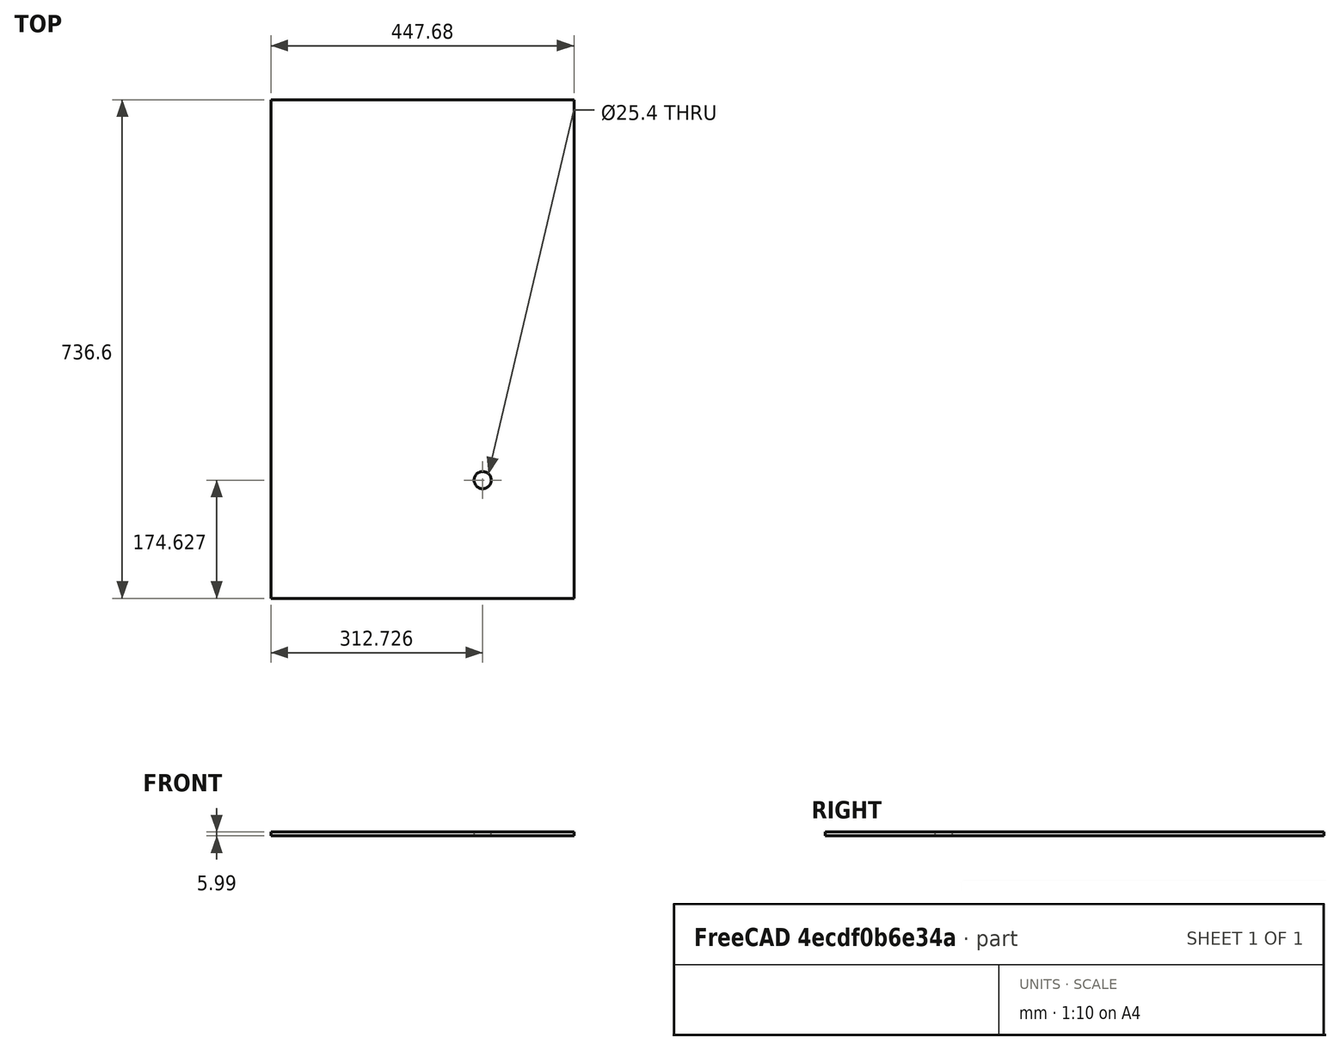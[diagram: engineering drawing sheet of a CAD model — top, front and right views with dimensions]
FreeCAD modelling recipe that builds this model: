
FCSTD DOCUMENT  (FreeCAD 0.19R24267 (Git))
Label: Inv1-P12
License: All rights reserved
LicenseURL: http://en.wikipedia.org/wiki/All_rights_reserved
objects: TechDraw::DrawViewDimension×6, TechDraw::DrawProjGroupItem×2, TechDraw::DrawHatch×2, TechDraw::DrawViewAnnotation×2, Sketcher::SketchObject×1, Part::Extrusion×1, TechDraw::DrawSVGTemplate×1, TechDraw::DrawProjGroup×1, TechDraw::DrawPage×1
note: 2 computed .brp shape members not serialized (recipe doc carries the construction recipe); baked Part::Feature solids carry a one-line shape summary decoded from their .brp

FEATURE [Sketcher::SketchObject] Sketch
  FullyConstrained = false
  sketch-geometry (5):
    g0: LineSegment StartX=-121.759 StartY=252.582 StartZ=0 EndX=325.916 EndY=252.582 EndZ=0
    g1: LineSegment StartX=325.916 StartY=252.582 StartZ=0 EndX=325.916 EndY=-484.018 EndZ=0
    g2: LineSegment StartX=325.916 StartY=-484.018 StartZ=0 EndX=-121.759 EndY=-484.018 EndZ=0
    g3: LineSegment StartX=-121.759 StartY=-484.018 StartZ=0 EndX=-121.759 EndY=252.582 EndZ=0
    g4: Circle CenterX=190.966 CenterY=-309.393 CenterZ=0 NormalX=0 NormalY=0 NormalZ=1 AngleXU=0 Radius=12.7
  constraints (13):
    c: Coincident(g0,g1)
    c: Coincident(g1,g2)
    c: Coincident(g2,g3)
    c: Coincident(g3,g0)
    c: Horizontal(g0)
    c: Horizontal(g2)
    c: Vertical(g1)
    c: Vertical(g3)
    c: DistanceX(g0,g0) = 447.675
    c: DistanceY(g3,g3) = 736.6
    c: Distance(g4,g1) = 134.95
    c: Distance(g4,g2) = 174.625
    c: Diameter(g4) = 25.4
FEATURE [Part::Extrusion] Extrude
  Base = -> Sketch
  Dir = (0,0,1)
  DirMode = 2
  FaceMakerClass = Part::FaceMakerBullseye
  LengthFwd = 5.9944
  LengthRev = 0
  Solid = true
  Symmetric = false
FEATURE [TechDraw::DrawSVGTemplate] Template
  Height = 215.9
  Orientation = 1
  Width = 279.4
FEATURE [TechDraw::DrawProjGroupItem] ProjItem  label="Front"
  CoarseView = false
  Direction = (0,0,1)
  Focus = 100
  HardHidden = false
  IsoCount = 0
  IsoHidden = false
  IsoVisible = false
  LockPosition = true
  Perspective = false
  Rotation = 0
  RotationVector = (1,0,0)
  Scale = 0.2
  ScaleType = 2
  SeamHidden = false
  SeamVisible = true
  SmoothHidden = false
  SmoothVisible = true
  Source = -> [Extrude]
  Type = 0
  X = 0
  XDirection = (1,0,0)
  Y = 0
FEATURE [TechDraw::DrawProjGroupItem] ProjItem001  label="Left"
  CoarseView = false
  Direction = (-1,0,1e-16)
  Focus = 100
  HardHidden = false
  IsoCount = 0
  IsoHidden = false
  IsoVisible = false
  LockPosition = false
  Perspective = false
  Rotation = 0
  RotationVector = (1,0,0)
  Scale = 0.2
  ScaleType = 2
  SeamHidden = false
  SeamVisible = true
  SmoothHidden = false
  SmoothVisible = true
  Source = -> [Extrude]
  Type = 1
  X = 81.5403
  XDirection = (1e-16,0,1)
  Y = 0
FEATURE [TechDraw::DrawProjGroup] ProjGroup
  Anchor = -> ProjItem
  AutoDistribute = true
  LockPosition = false
  ProjectionType = 0
  Rotation = 0
  Scale = 0.2
  ScaleType = 2
  Source = -> [Extrude]
  Views = -> [ProjItem,ProjItem001]
  X = 129.402
  Y = 104.062
  spacingX = 15.0114
  spacingY = 15.0114
FEATURE [TechDraw::DrawHatch] Hatch  label="HatchF0"
  HatchPattern = <path>
  Source = -> ProjItem [Face0]
FEATURE [TechDraw::DrawHatch] Hatch001  label="Hatch001F0"
  HatchPattern = <path>
  Source = -> ProjItem001 [Face0]
FEATURE [TechDraw::DrawViewDimension] Dimension
  Arbitrary = false
  ArbitraryTolerances = false
  EqualTolerance = true
  FormatSpec = %.3f
  FormatSpecOverTolerance = %+.3f
  FormatSpecUnderTolerance = %+.3f
  Inverted = false
  LockPosition = false
  MeasureType = 1
  OverTolerance = 0
  References2D = -> [ProjItem]
  Rotation = 0
  ScaleType = 0
  TheoreticalExact = false
  Type = 1
  UnderTolerance = 0
  X = 0
  Y = 86.0182
FEATURE [TechDraw::DrawViewDimension] Dimension001
  Arbitrary = false
  ArbitraryTolerances = false
  EqualTolerance = true
  FormatSpec = %.3f
  FormatSpecOverTolerance = %+.3f
  FormatSpecUnderTolerance = %+.3f
  Inverted = false
  LockPosition = false
  MeasureType = 1
  OverTolerance = 0
  References2D = -> [ProjItem]
  Rotation = 0
  ScaleType = 0
  TheoreticalExact = false
  Type = 2
  UnderTolerance = 0
  X = 53.1534
  Y = 0
FEATURE [TechDraw::DrawViewDimension] Dimension002
  Arbitrary = false
  ArbitraryTolerances = false
  EqualTolerance = true
  FormatSpec = ⌀%.3f
  FormatSpecOverTolerance = %+.3f
  FormatSpecUnderTolerance = %+.3f
  Inverted = false
  LockPosition = false
  MeasureType = 1
  OverTolerance = 0
  References2D = -> [ProjItem]
  Rotation = 0
  ScaleType = 0
  TheoreticalExact = false
  Type = 5
  UnderTolerance = 0
  X = 4.87778
  Y = -18.4764
FEATURE [TechDraw::DrawViewDimension] Dimension003
  Arbitrary = false
  ArbitraryTolerances = false
  EqualTolerance = true
  FormatSpec = %.3f
  FormatSpecOverTolerance = %+.3f
  FormatSpecUnderTolerance = %+.3f
  Inverted = false
  LockPosition = false
  MeasureType = 1
  OverTolerance = 0
  References2D = -> [ProjItem]
  Rotation = 0
  ScaleType = 0
  TheoreticalExact = false
  Type = 1
  UnderTolerance = 0
  X = 30.5675
  Y = -26.4256
FEATURE [TechDraw::DrawViewDimension] Dimension004
  Arbitrary = false
  ArbitraryTolerances = false
  EqualTolerance = true
  FormatSpec = %.3f
  FormatSpecOverTolerance = %+.3f
  FormatSpecUnderTolerance = %+.3f
  Inverted = false
  LockPosition = false
  MeasureType = 1
  OverTolerance = 0
  References2D = -> [ProjItem]
  Rotation = 0
  ScaleType = 0
  TheoreticalExact = false
  Type = 2
  UnderTolerance = 0
  X = 5.92496
  Y = -54.6431
FEATURE [TechDraw::DrawViewDimension] Dimension005
  Arbitrary = false
  ArbitraryTolerances = false
  EqualTolerance = true
  FormatSpec = %.3f
  FormatSpecOverTolerance = %+.3f
  FormatSpecUnderTolerance = %+.3f
  Inverted = false
  LockPosition = false
  MeasureType = 1
  OverTolerance = 0
  References2D = -> [ProjItem001]
  Rotation = 0
  ScaleType = 0
  TheoreticalExact = false
  Type = 1
  UnderTolerance = 0
  X = 15.397
  Y = 56.0389
FEATURE [TechDraw::DrawViewAnnotation] Annotation002
  Font = osifont
  LineSpace = 80
  LockPosition = false
  MaxWidth = -1
  Rotation = 0
  ScaleType = 0
  Text = Units: Inches
  TextSize = 5.0038
  TextStyle = 0
  X = 259.08
  Y = 5.08
FEATURE [TechDraw::DrawViewAnnotation] Annotation
  Font = osifont
  LineSpace = 80
  LockPosition = false
  MaxWidth = -1
  Rotation = 0
  ScaleType = 0
  Text = Figure S1 (Inverted 1) |  Panel 12 [back] | Quantity: 1
  TextSize = 5.0038
  TextStyle = 0
  X = 32.0848
  Y = 195.58
FEATURE [TechDraw::DrawPage] Page
  KeepUpdated = true
  NextBalloonIndex = 1
  ProjectionType = 0
  Template = -> Template
  Views = -> [ProjGroup,Dimension,Dimension001,Dimension002,Dimension003,Dimension004,Dimension005,Annotation,Annotation002]
note: 2 file-system paths scrubbed to <path> (originals preserved in the JSON sidecar)
